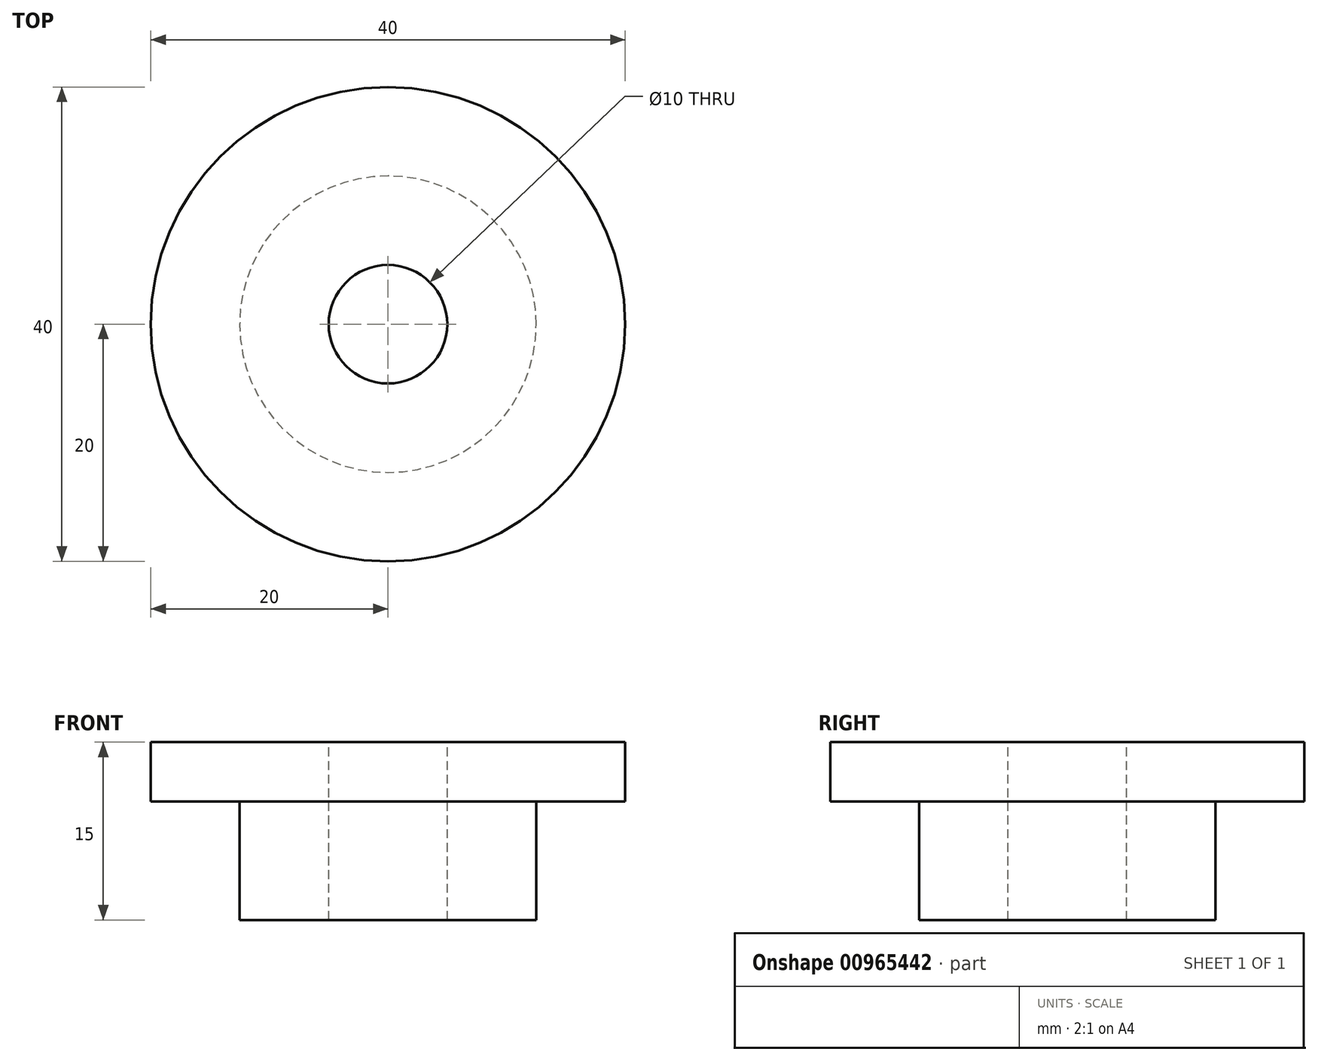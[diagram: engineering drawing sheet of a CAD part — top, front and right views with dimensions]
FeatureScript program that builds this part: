
annotation { "Feature Type Name" : "Feature", "Feature Type Description" : "" }
export const myFeature = defineFeature(function(context is Context, id is Id, definition is map)
    precondition{}
    {
        {
            var Q0;
            Q0=qCreatedBy(makeId("Front.planeOp"),FACE);
            var sketch = newSketch(context, id + "F0", { "sketchPlane" : qUnion([Q0])});
            skLineSegment(sketch, "E0", {"start": v(0, 10) * mm, "end": v(0, -20) * mm, "construction": true});
            skLineSegment(sketch, "E1.top", {"start": v(0, 2.5) * mm, "end": v(-20, 2.5) * mm});
            skLineSegment(sketch, "E1.right", {"start": v(-20, -2.5) * mm, "end": v(-20, 2.5) * mm});
            skPoint(sketch, "E1.middle", {"position": v(0, 0) * mm});
            skLineSegment(sketch, "E2.top", {"start": v(0, -12.5) * mm, "end": v(-12.5, -12.5) * mm});
            skLineSegment(sketch, "E2.right", {"start": v(-12.5, -2.5) * mm, "end": v(-12.5, -12.5) * mm});
            skPoint(sketch, "E2.middle", {"position": v(0, -7.5) * mm});
            skLineSegment(sketch, "E3.trimOffspring", {"start": v(-12.5, -2.5) * mm, "end": v(-20, -2.5) * mm});
            skLineSegment(sketch, "E4", {"start": v(0, 2.5) * mm, "end": v(0, -12.5) * mm});
            skPoint(sketch, "E2.left.end.orphan", {"position": v(12.5, -12.5) * mm});
            skPoint(sketch, "E1.bottom.end.orphan", {"position": v(12.5, -2.5) * mm});
            skPoint(sketch, "E1.left.start.orphan", {"position": v(20, -2.5) * mm});
            skPoint(sketch, "E5.orphan", {"position": v(20, 2.5) * mm});
            skSolve(sketch);
        }
        {
            var Q0;
            Q0 = qSketchRegion(id + "F0", true);
            var Q1;
            Q1=sQuery(id+"F0.wireOp",EDGE,"E0");
            revolve(context, id + "F1", {"surfaceOperationType" : NewSurfaceOperationType.NEW, "entities" : qUnion([Q0]), "axis" : qUnion([Q1]), "revolveType" : RevolveType.FULL});
        }
        {
            var Q0;
            Q0=makeQuery(id+"F1.opRevolve","SWEPT_FACE",FACE,{"disambiguationData":[OSD([sQuery(id+"F0.wireOp",EDGE,"E1.top")])]});
            var sketch = newSketch(context, id + "F2", { "sketchPlane" : qUnion([Q0])});
            skCircle(sketch, "E6", {"center": v(0, 0) * mm, "radius": 5 * mm});
            skSolve(sketch);
        }
        {
            var Q0;
            Q0 = qSketchRegion(id + "F2", true);
            extrude(context, id + "F3", {"entities" : qUnion([Q0]), "operationType" : NewBodyOperationType.REMOVE, "oppositeDirection" : true, "depth" : 25 * mm, "offsetDistance" : 25 * mm});
        }
    });
